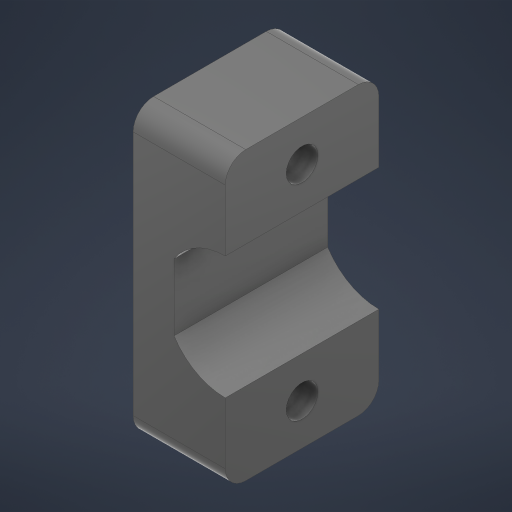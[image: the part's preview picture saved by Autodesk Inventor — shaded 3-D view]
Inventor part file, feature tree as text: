
AUTODESK INVENTOR PART (.ipt)
format: ipt  version: 2024 (Build 280153000, 153)  size: 231,424 bytes
history: native  units: in
note: dims shown in document units (in); Inventor stores cm internally (conversion verified against a paired STEP export)
features: sketch x2, extrude x1, plane x1, hole x1, fillet x1
ambient origin geometry x8: Origin, YZ Plane, XZ Plane, XY Plane, X Axis, Y Axis, Z Axis, Center Point
bodies: Body1 (feature_tree)
feature tree (6):
  extrude  "Extrusion2"  Depth=0.3543in
  plane  "Work Plane1"
  hole  "Hole1"  [1 undecoded]
  fillet  "Fillet1"  Radius=0.1575in
  sketch  "Sketch2"  dims[d8=0.5906in d9=0.0in d10=0.3543in]
  sketch  "Sketch3"  dims[d11=0.1575in d16=0.2953in d17=0.1575in d18=0.1575in d19=0.2953in d20=0.122in d21=0.2362in d22=0.1575in d23=0.0787in d24=90.0deg d25=0.315in d26=0.8108in d27=0.0787in]
note: 1 required parameter value undecoded (feature->parameter linkage not recoverable at this tier; creation-order binding heuristic only, values carry confidence <= 0.55)
